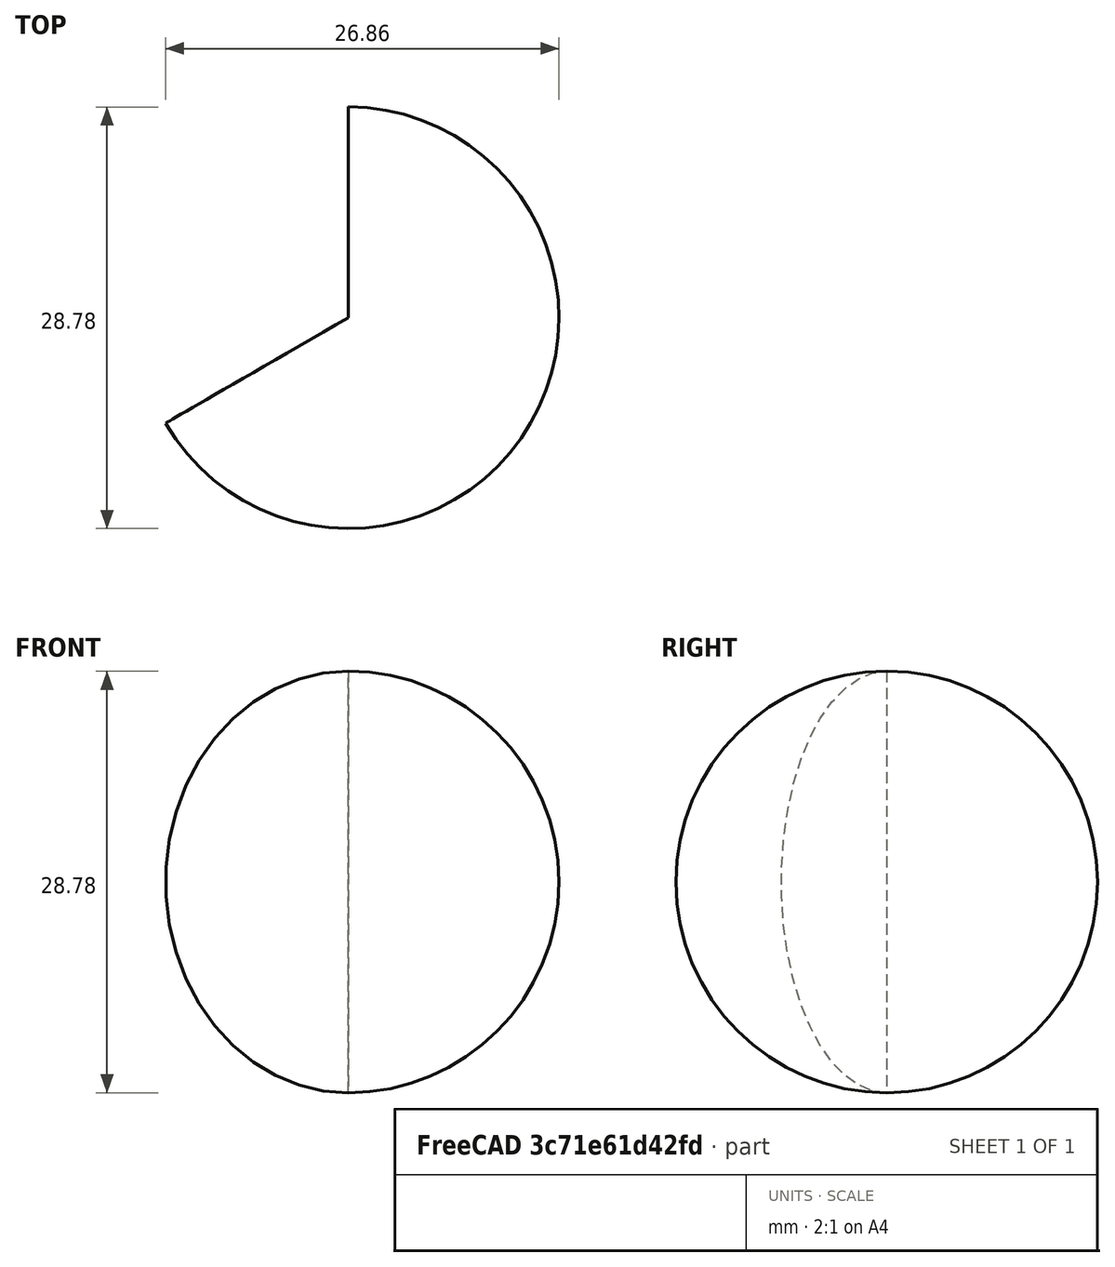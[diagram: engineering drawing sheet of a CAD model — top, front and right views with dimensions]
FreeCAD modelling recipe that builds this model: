
FCSTD DOCUMENT  (FreeCAD 1.0R38806 (Git))
Label: ExtrusionAial
License: All rights reserved
LicenseURL: http://en.wikipedia.org/wiki/All_rights_reserved
objects: Sketcher::SketchObject×1, PartDesign::Revolution×1, PartDesign::Body×1
note: 6 computed .brp shape members not serialized (recipe doc carries the construction recipe); baked Part::Feature solids carry a one-line shape summary decoded from their .brp

FEATURE [Sketcher::SketchObject] Sketch
  ArcFitTolerance = 1e-06
  AttachmentSupport = -> [YZ_Plane]
  FullyConstrained = false
  MakeInternals = false
  MapMode = 5
  Placement = pos=(0,0,0) rot=(0.57735,0.57735,0.57735;2.0944rad)
  sketch-geometry (2):
    g0: ArcOfCircle CenterX=0 CenterY=0 CenterZ=0 NormalX=0 NormalY=0 NormalZ=1 AngleXU=0 Radius=14.3939 StartAngle=4.71239 EndAngle=7.85398
    g1: LineSegment StartX=0 StartY=14.3939 StartZ=0 EndX=0 EndY=-14.3939 EndZ=0
  constraints (5):
    c: Coincident(g0,g-1)
    c: PointOnObject(g0,g-2)
    c: PointOnObject(g0,g-2)
    c: Coincident(g1,g0)
    c: Coincident(g1,g0)
FEATURE [PartDesign::Revolution] Revolution
  Angle = 240
  Angle2 = 60
  Axis = (0,0,1)
  Base = (0,0,0)
  Placement = pos=(0,0,0) rot=(1,1,1;2.0944rad)
  Profile = -> Sketch
  ReferenceAxis = -> Sketch [V_Axis]
  Reversed = true
  Suppressed = false
  Type = 0
FEATURE [PartDesign::Body] Body
  AllowCompound = false
  Group = -> [Sketch,Revolution]
  Origin = -> Origin
  Tip = -> Revolution
